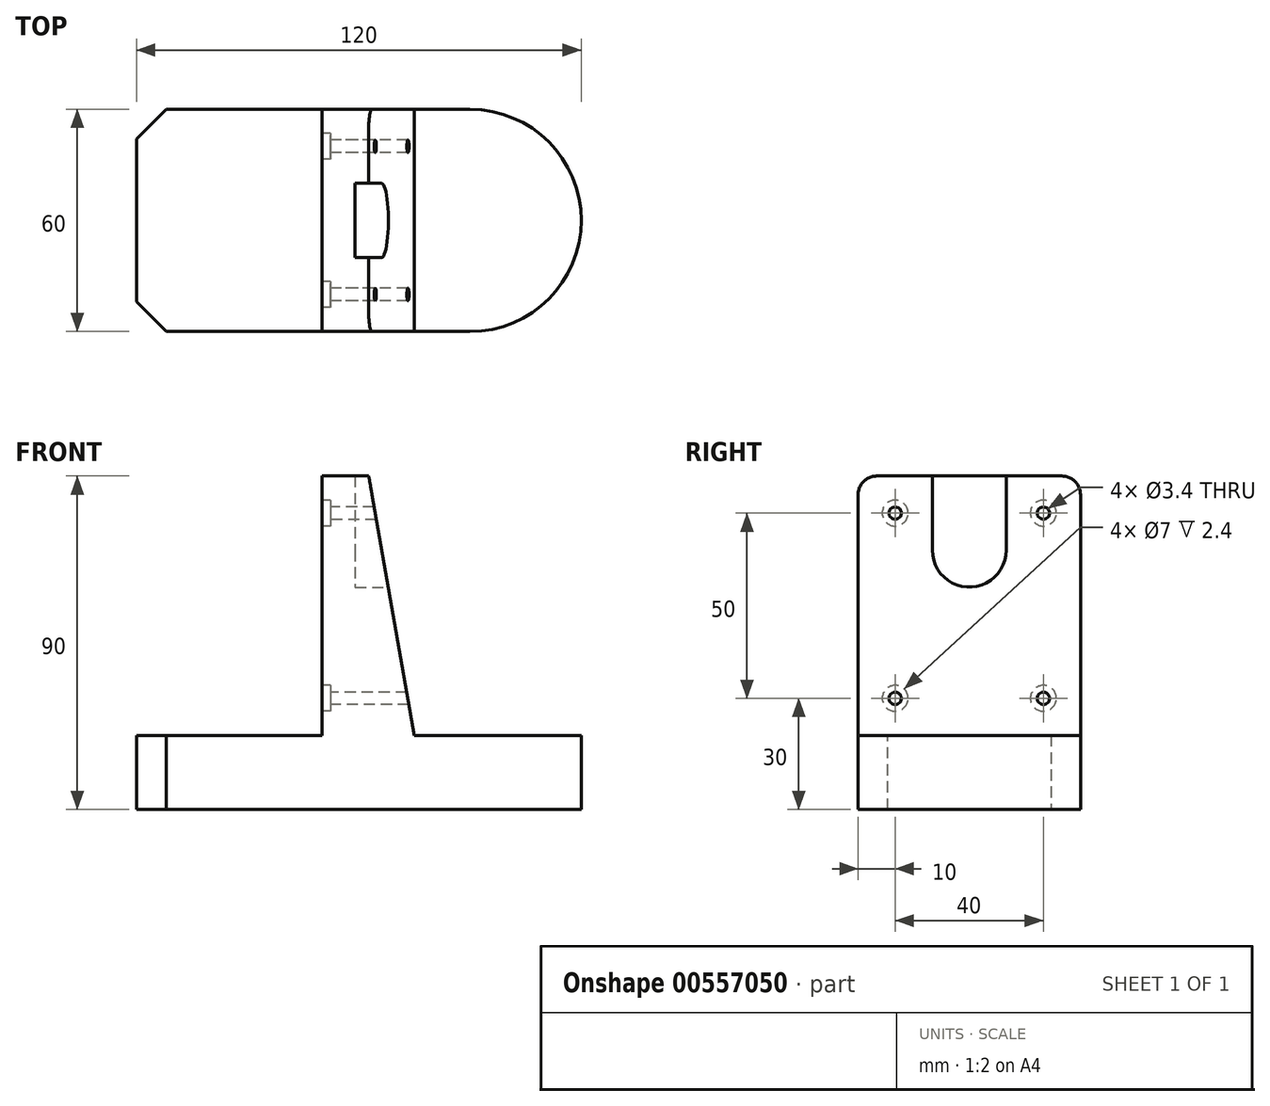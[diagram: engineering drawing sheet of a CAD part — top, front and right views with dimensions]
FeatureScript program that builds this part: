
annotation { "Feature Type Name" : "Feature", "Feature Type Description" : "" }
export const myFeature = defineFeature(function(context is Context, id is Id, definition is map)
    precondition{}
    {
        {
            var Q0;
            Q0=qCreatedBy(makeId("Top.planeOp"),FACE);
            var sketch = newSketch(context, id + "F0", { "sketchPlane" : qUnion([Q0])});
            skLineSegment(sketch, "E0.bottom", {"start": v(0, 0) * mm, "end": v(120, 0) * mm});
            skLineSegment(sketch, "E0.top", {"start": v(0, 60) * mm, "end": v(120, 60) * mm});
            skLineSegment(sketch, "E0.left", {"start": v(0, 0) * mm, "end": v(0, 60) * mm});
            skLineSegment(sketch, "E0.right", {"start": v(120, 0) * mm, "end": v(120, 60) * mm});
            skSolve(sketch);
        }
        {
            var Q0;
            Q0=makeQuery(id+"F0.imprint","IMPRINT",FACE,{"disambiguationData":[TD([[makeQuery(id+"F0.imprint","IMPRINT",EDGE,{"derivedFrom":sQuery(id+"F0.wireOp",EDGE,"E0.bottom")}),1.0]])]});
            extrude(context, id + "F1", {"entities" : qUnion([Q0]), "depth" : 90 * mm, "offsetDistance" : 25 * mm});
        }
        {
            var Q0;
            Q0=makeQuery(id+"F1.opExtrude","SWEPT_FACE",FACE,{"disambiguationData":[OSD([sQuery(id+"F0.wireOp",EDGE,"E0.bottom")])]});
            var sketch = newSketch(context, id + "F2", { "sketchPlane" : qUnion([Q0])});
            skLineSegment(sketch, "E1", {"start": v(0, 20) * mm, "end": v(120, 20) * mm});
            skLineSegment(sketch, "E2", {"start": v(50, 90) * mm, "end": v(50, 20) * mm});
            skLineSegment(sketch, "E3", {"start": v(75, 90) * mm, "end": v(75, 20) * mm});
            skSolve(sketch);
        }
        {
            var Q0;
            {var subQ4=sQuery(id+"F2.wireOp",EDGE,"E2");Q0=makeQuery(id+"F2.imprint","IMPRINT",FACE,{"disambiguationData":[TD([[makeQuery(id+"F2.imprint","IMPRINT",EDGE,{"derivedFrom":subQ4}),-1.0]])]});}
            var Q1;
            {var subQ4=sQuery(id+"F2.wireOp",EDGE,"E3");Q1=makeQuery(id+"F2.imprint","IMPRINT",FACE,{"disambiguationData":[TD([[makeQuery(id+"F2.imprint","IMPRINT",EDGE,{"derivedFrom":subQ4}),1.0]])]});}
            extrude(context, id + "F3", {"entities" : qUnion([Q0, Q1]), "operationType" : NewBodyOperationType.REMOVE, "endBound" : BoundingType.THROUGH_ALL, "oppositeDirection" : true, "depth" : 25 * mm, "offsetDistance" : 25 * mm});
        }
        {
            var Q0;
            Q0=makeQuery(id+"F1.opExtrude","SWEPT_EDGE",EDGE,{"disambiguationData":[OSD([sQuery(id+"F0.wireOp",EDGE,"E0.top"),sQuery(id+"F0.wireOp",EDGE,"E0.right")])]});
            var Q1;
            Q1=makeQuery(id+"F1.opExtrude","SWEPT_EDGE",EDGE,{"disambiguationData":[OSD([sQuery(id+"F0.wireOp",EDGE,"E0.bottom"),sQuery(id+"F0.wireOp",EDGE,"E0.right")])]});
            fillet(context, id + "F4", {"entities" : qUnion([Q0, Q1]), "radius" : 30 * mm, "tangentPropagation" : true, "allowEdgeOverflow" : false});
        }
        {
            var Q0;
            Q0=makeQuery(id+"F1.opExtrude","SWEPT_EDGE",EDGE,{"disambiguationData":[OSD([sQuery(id+"F0.wireOp",EDGE,"E0.top"),sQuery(id+"F0.wireOp",EDGE,"E0.left")])]});
            var Q1;
            Q1=makeQuery(id+"F1.opExtrude","SWEPT_EDGE",EDGE,{"disambiguationData":[OSD([sQuery(id+"F0.wireOp",EDGE,"E0.bottom"),sQuery(id+"F0.wireOp",EDGE,"E0.left")])]});
            chamfer(context, id + "F5", {"entities" : qUnion([Q0, Q1]), "width" : 8 * mm, "tangentPropagation" : true});
        }
        {
            var Q0;
            Q0=makeQuery(id+"F3.boolean.opBoolean","COPY",FACE,{"derivedFrom":makeQuery(id+"F3.opExtrude","SWEPT_FACE",FACE,{"disambiguationData":[OSD([sQuery(id+"F2.wireOp",EDGE,"E2")])]})});
            var sketch = newSketch(context, id + "F6", { "sketchPlane" : qUnion([Q0])});
            skLineSegment(sketch, "E4.bottom", {"start": v(-50, 80) * mm, "end": v(-10, 80) * mm});
            skLineSegment(sketch, "E4.top", {"start": v(-50, 30) * mm, "end": v(-10, 30) * mm});
            skLineSegment(sketch, "E4.left", {"start": v(-50, 80) * mm, "end": v(-50, 30) * mm});
            skLineSegment(sketch, "E4.right", {"start": v(-10, 80) * mm, "end": v(-10, 30) * mm});
            skPoint(sketch, "E5", {"position": v(-50, 80) * mm});
            skPoint(sketch, "E6", {"position": v(-10, 80) * mm});
            skPoint(sketch, "E7", {"position": v(-50, 30) * mm});
            skPoint(sketch, "E8", {"position": v(-10, 30) * mm});
            skSolve(sketch);
        }
        {
            var Q0;
            Q0=sQuery(id+"F6.wireOp",VERTEX,"E5");
            var Q1;
            Q1=sQuery(id+"F6.wireOp",VERTEX,"E6");
            var Q2;
            Q2=sQuery(id+"F6.wireOp",VERTEX,"E8");
            var Q3;
            Q3=sQuery(id+"F6.wireOp",VERTEX,"E7");
            var Q4;
            Q4=makeQuery(id+"F1.opExtrude","SWEPT_BODY",BODY,{"disambiguationData":[OSD([sQuery(id+"F0.wireOp",EDGE,"E0.bottom"),sQuery(id+"F0.wireOp",EDGE,"E0.top"),sQuery(id+"F0.wireOp",EDGE,"E0.left"),sQuery(id+"F0.wireOp",EDGE,"E0.right")])]});
            hole(context, id + "F7", {"style" : HoleStyle.C_BORE, "endStyle" : HoleEndStyle.THROUGH, "holeDiameter" : 3.4 * mm, "cBoreDiameter" : 7 * mm, "cBoreDepth" : 2.4 * mm, "isTappedThrough" : true, "tappedDepth" : 12 * mm, "tapClearance" : 3, "locations" : qUnion([Q0, Q1, Q2, Q3]), "scope" : qUnion([Q4])});
        }
        {
            var Q0;
            Q0=makeQuery(id+"F3.boolean.opBoolean","COPY",FACE,{"derivedFrom":makeQuery(id+"F3.opExtrude","SWEPT_FACE",FACE,{"disambiguationData":[OSD([sQuery(id+"F2.wireOp",EDGE,"E3")])]})});
            var sketch = newSketch(context, id + "F8", { "sketchPlane" : qUnion([Q0])});
            skLineSegment(sketch, "E9.bottom", {"start": v(20, 90) * mm, "end": v(40, 90) * mm});
            skLineSegment(sketch, "E9.top", {"start": v(20, 70) * mm, "end": v(40, 70) * mm});
            skLineSegment(sketch, "E9.left", {"start": v(20, 90) * mm, "end": v(20, 70) * mm});
            skLineSegment(sketch, "E9.right", {"start": v(40, 90) * mm, "end": v(40, 70) * mm});
            skCircle(sketch, "E10", {"center": v(30, 70) * mm, "radius": 10 * mm});
            skSolve(sketch);
        }
        {
            var Q0;
            Q0=makeQuery(id+"F8.imprint","IMPRINT",FACE,{"disambiguationData":[TD([[makeQuery(id+"F8.imprint","IMPRINT",EDGE,{"derivedFrom":sQuery(id+"F8.wireOp",EDGE,"E9.bottom")}),1.0]])]});
            var Q1;
            {var subQ0=sQuery(id+"F8.wireOp",EDGE,"E9.top");Q1=makeQuery(id+"F8.imprint","IMPRINT",FACE,{"disambiguationData":[TD([[makeQuery(id+"F8.imprint","IMPRINT",EDGE,{"derivedFrom":subQ0}),1.0]])]});}
            var Q2;
            {var subQ0=sQuery(id+"F8.wireOp",EDGE,"E9.top");Q2=makeQuery(id+"F8.imprint","IMPRINT",FACE,{"disambiguationData":[TD([[makeQuery(id+"F8.imprint","IMPRINT",EDGE,{"derivedFrom":subQ0}),-1.0]])]});}
            extrude(context, id + "F9", {"entities" : qUnion([Q0, Q1, Q2]), "operationType" : NewBodyOperationType.REMOVE, "oppositeDirection" : true, "depth" : 16 * mm, "offsetDistance" : 25 * mm});
        }
        {
            var Q0;
            Q0=makeQuery(id+"F1.opExtrude","SWEPT_FACE",FACE,{"disambiguationData":[OSD([sQuery(id+"F0.wireOp",EDGE,"E0.bottom")])]});
            var sketch = newSketch(context, id + "F10", { "sketchPlane" : qUnion([Q0])});
            skLineSegment(sketch, "E11", {"start": v(75, 20) * mm, "end": v(62.66, 90) * mm});
            skSolve(sketch);
        }
        {
            var Q0;
            {var subQ0=sQuery(id+"F10.wireOp",EDGE,"E11");Q0=makeQuery(id+"F10.imprint","IMPRINT",FACE,{"disambiguationData":[TD([[makeQuery(id+"F10.imprint","IMPRINT",EDGE,{"derivedFrom":subQ0}),-1.0]])]});}
            extrude(context, id + "F11", {"entities" : qUnion([Q0]), "operationType" : NewBodyOperationType.REMOVE, "endBound" : BoundingType.THROUGH_ALL, "oppositeDirection" : true, "depth" : 25 * mm, "offsetDistance" : 25 * mm});
        }
        {
            var Q0;
            Q0=makeQuery(id+"F1.opExtrude","CAP_EDGE",EDGE,{"disambiguationData":[OSD([sQuery(id+"F0.wireOp",EDGE,"E0.top")])],"isStart":false});
            var Q1;
            Q1=makeQuery(id+"F1.opExtrude","CAP_EDGE",EDGE,{"disambiguationData":[OSD([sQuery(id+"F0.wireOp",EDGE,"E0.bottom")])],"isStart":false});
            fillet(context, id + "F12", {"entities" : qUnion([Q0, Q1]), "radius" : 5 * mm, "tangentPropagation" : true, "allowEdgeOverflow" : false});
        }
    });
